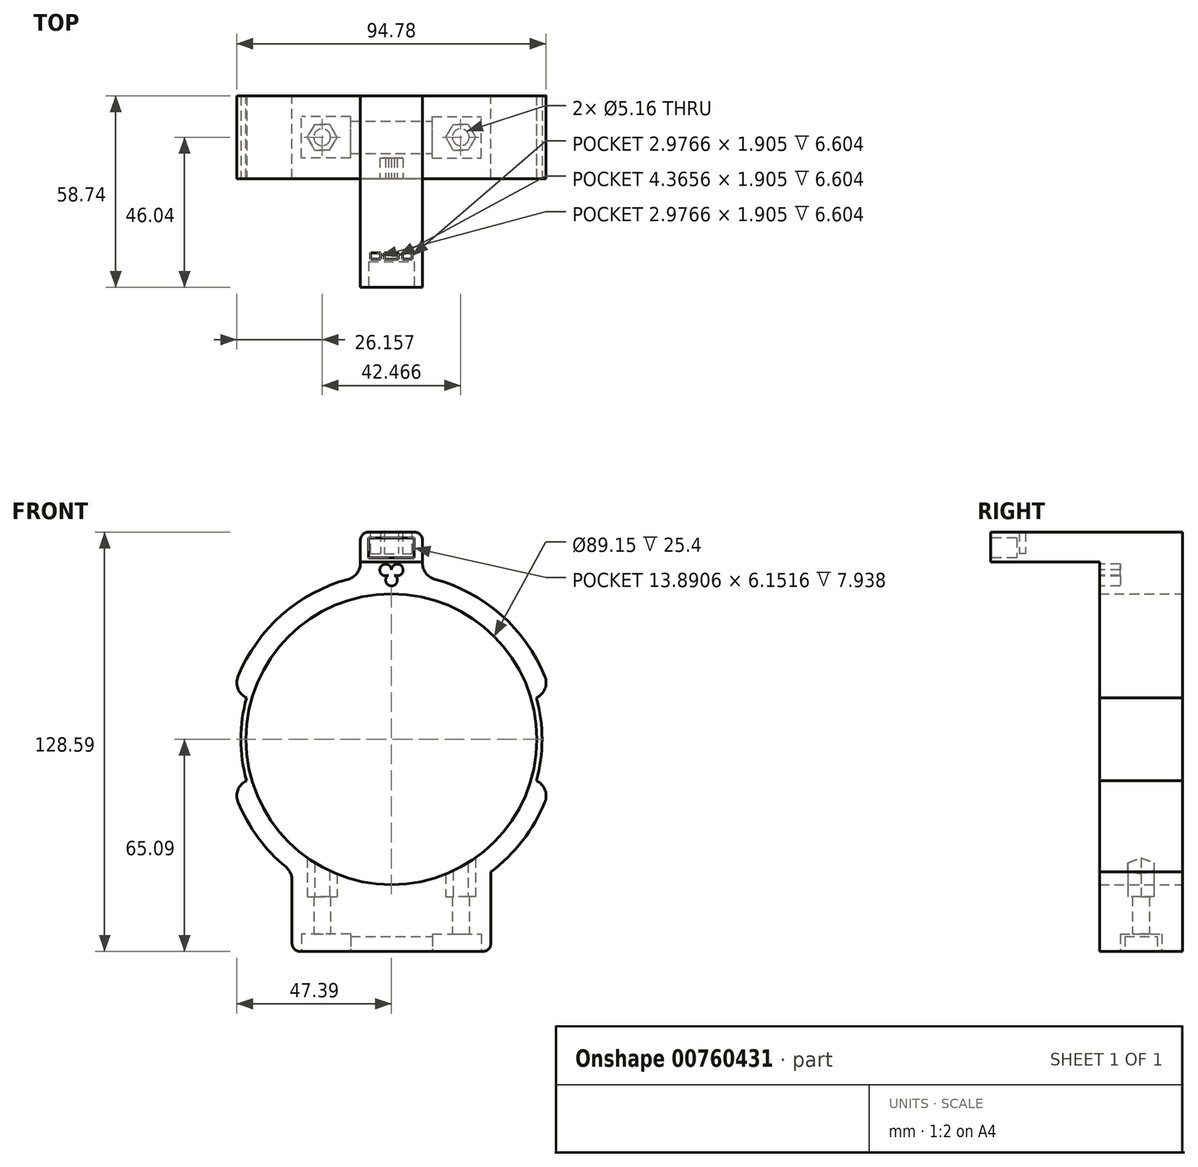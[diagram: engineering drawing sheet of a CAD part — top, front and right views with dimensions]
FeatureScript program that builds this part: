
annotation { "Feature Type Name" : "Feature", "Feature Type Description" : "" }
export const myFeature = defineFeature(function(context is Context, id is Id, definition is map)
    precondition{}
    {
        {
            var Q0;
            Q0=qCreatedBy(makeId("Front.planeOp"),FACE);
            var sketch = newSketch(context, id + "F0", { "sketchPlane" : qUnion([Q0])});
            skCircle(sketch, "E0", {"center": v(0, 0) * mm, "radius": 44.58 * mm});
            skCircle(sketch, "E1", {"center": v(0, 0) * mm, "radius": 50.8 * mm});
            skLineSegment(sketch, "E2.bottom", {"start": v(-9.52, 0) * mm, "end": v(9.53, 0) * mm});
            skLineSegment(sketch, "E2.top", {"start": v(-9.53, 63.5) * mm, "end": v(9.52, 63.5) * mm});
            skLineSegment(sketch, "E2.left", {"start": v(-9.52, 0) * mm, "end": v(-9.53, 63.5) * mm});
            skLineSegment(sketch, "E2.right", {"start": v(9.53, 0) * mm, "end": v(9.52, 63.5) * mm});
            skSolve(sketch);
        }
        {
            var Q0;
            {var subQ0=sQuery(id+"F0.wireOp",EDGE,"E2.left");var subQ1=sQuery(id+"F0.wireOp",EDGE,"E0");var subQ2=makeQuery(id+"F0.imprint","INTERSECT",VERTEX,{"derivedFrom":[subQ1,subQ0]});Q0=makeQuery(id+"F0.imprint","IMPRINT",FACE,{"disambiguationData":[TD([[makeQuery(id+"F0.imprint","IMPRINT",EDGE,{"disambiguationData":[TD([[subQ2,-1.0]])],"derivedFrom":subQ1}),-1.0]])]});}
            var Q1;
            {var subQ0=sQuery(id+"F0.wireOp",EDGE,"E2.left");var subQ1=sQuery(id+"F0.wireOp",EDGE,"E0");var subQ2=makeQuery(id+"F0.imprint","INTERSECT",VERTEX,{"derivedFrom":[subQ1,subQ0]});Q1=makeQuery(id+"F0.imprint","IMPRINT",FACE,{"disambiguationData":[TD([[makeQuery(id+"F0.imprint","IMPRINT",EDGE,{"disambiguationData":[TD([[subQ2,1.0]])],"derivedFrom":subQ1}),-1.0]])]});}
            var Q2;
            {var subQ5=sQuery(id+"F0.wireOp",EDGE,"E2.top");Q2=makeQuery(id+"F0.imprint","IMPRINT",FACE,{"disambiguationData":[TD([[makeQuery(id+"F0.imprint","IMPRINT",EDGE,{"derivedFrom":subQ5}),-1.0]])]});}
            extrude(context, id + "F1", {"entities" : qUnion([Q0, Q1, Q2]), "depth" : 25.4 * mm, "offsetDistance" : 25.4 * mm});
        }
        {
            var Q0;
            Q0=makeQuery(id+"F1.opExtrude","CAP_FACE",FACE,{"disambiguationData":[OSD([sQuery(id+"F0.wireOp",EDGE,"E0"),sQuery(id+"F0.wireOp",EDGE,"E1"),sQuery(id+"F0.wireOp",EDGE,"E2.top"),sQuery(id+"F0.wireOp",EDGE,"E2.left"),sQuery(id+"F0.wireOp",EDGE,"E2.right")])],"isStart":false});
            var sketch = newSketch(context, id + "F2", { "sketchPlane" : qUnion([Q0])});
            skCircle(sketch, "E3", {"center": v(1.79, 51.87) * mm, "radius": 1.79 * mm});
            skCircle(sketch, "E4.MirrorC", {"center": v(-1.79, 51.87) * mm, "radius": 1.79 * mm});
            skCircle(sketch, "E5", {"center": v(0, 48.78) * mm, "radius": 1.79 * mm});
            skSolve(sketch);
        }
        {
            var Q0;
            Q0=qSketchRegion(id+"F2",true);
            extrude(context, id + "F3", {"entities" : qUnion([Q0]), "operationType" : NewBodyOperationType.REMOVE, "oppositeDirection" : true, "depth" : 6.35 * mm, "offsetDistance" : 25.4 * mm});
        }
        {
            var Q0;
            Q0=qCreatedBy(makeId("Front.planeOp"),FACE);
            var sketch = newSketch(context, id + "F4", { "sketchPlane" : qUnion([Q0])});
            skLineSegment(sketch, "E6.bottom", {"start": v(30.48, -65.09) * mm, "end": v(-30.48, -65.09) * mm});
            skLineSegment(sketch, "E7", {"start": v(-30.48, -65.09) * mm, "end": v(-30.48, -40.64) * mm});
            skLineSegment(sketch, "E8", {"start": v(30.48, -65.09) * mm, "end": v(30.48, -40.64) * mm});
            skArc(sketch, "E9", {"start": v(-30.48, -40.64) * mm, "mid": v(0, -50.8) * mm, "end": v(30.48, -40.64) * mm});
            skLineSegment(sketch, "E10", {"start": v(0, -50.8) * mm, "end": v(0, -75.8) * mm, "construction": true});
            skLineSegment(sketch, "E11", {"start": v(10.8, -65.09) * mm, "end": v(10.8, -75.8) * mm, "construction": true});
            skLineSegment(sketch, "E12", {"start": v(-41.35, -44.45) * mm, "end": v(48.58, -44.45) * mm, "construction": true});
            skSolve(sketch);
        }
        {
            var Q0;
            Q0=qSketchRegion(id+"F4",true);
            extrude(context, id + "F5", {"entities" : qUnion([Q0]), "operationType" : NewBodyOperationType.ADD, "depth" : 25.4 * mm, "offsetDistance" : 25.4 * mm});
        }
        {
            var Q0;
            Q0=makeQuery(id+"F5.opExtrude","SWEPT_FACE",FACE,{"disambiguationData":[OSD([sQuery(id+"F4.wireOp",EDGE,"E6.bottom")])]});
            var sketch = newSketch(context, id + "F6", { "sketchPlane" : qUnion([Q0])});
            skLineSegment(sketch, "E13.bottom", {"start": v(12.5, 19.05) * mm, "end": v(27.58, 19.05) * mm});
            skLineSegment(sketch, "E13.top", {"start": v(12.5, 6.35) * mm, "end": v(27.58, 6.35) * mm});
            skLineSegment(sketch, "E13.left", {"start": v(12.5, 19.05) * mm, "end": v(12.5, 6.35) * mm});
            skLineSegment(sketch, "E13.right", {"start": v(27.58, 19.05) * mm, "end": v(27.58, 6.35) * mm});
            skLineSegment(sketch, "E14.MirrorCS", {"start": v(-12.5, 19.05) * mm, "end": v(-27.58, 19.05) * mm});
            skLineSegment(sketch, "E15.MirrorCS", {"start": v(-12.5, 19.05) * mm, "end": v(-12.5, 6.35) * mm});
            skLineSegment(sketch, "E16.MirrorCS", {"start": v(-12.5, 6.35) * mm, "end": v(-27.58, 6.35) * mm});
            skLineSegment(sketch, "E17.MirrorCS", {"start": v(-27.58, 19.05) * mm, "end": v(-27.58, 6.35) * mm});
            skPoint(sketch, "E18.centerSnap0", {"position": v(12.5, 12.7) * mm});
            skSolve(sketch);
        }
        {
            var Q0;
            Q0=qSketchRegion(id+"F6",true);
            extrude(context, id + "F7", {"entities" : qUnion([Q0]), "operationType" : NewBodyOperationType.REMOVE, "oppositeDirection" : true, "depth" : 5.36 * mm, "offsetDistance" : 25.4 * mm});
        }
        {
            var Q0;
            Q0=makeQuery(id+"F7.boolean.opBoolean","COPY",FACE,{"derivedFrom":makeQuery(id+"F7.opExtrude","CAP_FACE",FACE,{"disambiguationData":[OSD([sQuery(id+"F6.wireOp",EDGE,"E13.bottom"),sQuery(id+"F6.wireOp",EDGE,"E13.top"),sQuery(id+"F6.wireOp",EDGE,"E13.left"),sQuery(id+"F6.wireOp",EDGE,"E13.right")])],"isStart":false})});
            var sketch = newSketch(context, id + "F8", { "sketchPlane" : qUnion([Q0])});
            skCircle(sketch, "E19", {"center": v(21.23, 12.7) * mm, "radius": 2.58 * mm});
            skPoint(sketch, "E19.centerSnap0", {"position": v(12.5, 12.7) * mm});
            skCircle(sketch, "E20.MirrorC", {"center": v(-21.23, 12.7) * mm, "radius": 2.58 * mm});
            skSolve(sketch);
        }
        {
            var Q0;
            Q0=qSketchRegion(id+"F8",true);
            extrude(context, id + "F9", {"entities" : qUnion([Q0]), "operationType" : NewBodyOperationType.REMOVE, "oppositeDirection" : true, "depth" : 25.4 * mm, "offsetDistance" : 25.4 * mm});
        }
        {
            var Q0;
            Q0=qCreatedBy(makeId("Top.planeOp"),FACE);
            cPlane(context, id + "F10", {"entities" : qUnion([Q0]), "cplaneType" : CPlaneType.OFFSET, "offset" : 48.26 * mm, "oppositeDirection" : true, "width" : 152.4 * mm, "height" : 152.4 * mm});
        }
        {
            var Q0;
            Q0=qCreatedBy(id+"F10.planeOp",FACE);
            var sketch = newSketch(context, id + "F11", { "sketchPlane" : qUnion([Q0])});
            skCircle(sketch, "E21.cCircle", {"center": v(21.23, -12.7) * mm, "radius": 3.97 * mm, "construction": true});
            skLineSegment(sketch, "E21.0", {"start": v(23.52, -16.67) * mm, "end": v(18.94, -16.67) * mm});
            skLineSegment(sketch, "E21.1", {"start": v(18.94, -16.67) * mm, "end": v(16.65, -12.7) * mm});
            skLineSegment(sketch, "E21.2", {"start": v(16.65, -12.7) * mm, "end": v(18.94, -8.73) * mm});
            skLineSegment(sketch, "E21.3", {"start": v(18.94, -8.73) * mm, "end": v(23.52, -8.73) * mm});
            skLineSegment(sketch, "E21.4", {"start": v(23.52, -8.73) * mm, "end": v(25.82, -12.7) * mm});
            skLineSegment(sketch, "E21.5", {"start": v(25.82, -12.7) * mm, "end": v(23.52, -16.67) * mm});
            skPoint(sketch, "E21.0.midPoint", {"position": v(21.23, -16.67) * mm});
            skLineSegment(sketch, "E22.MirrorCS", {"start": v(-23.52, -16.67) * mm, "end": v(-18.94, -16.67) * mm});
            skLineSegment(sketch, "E23.MirrorCS", {"start": v(-18.94, -16.67) * mm, "end": v(-16.65, -12.7) * mm});
            skLineSegment(sketch, "E24.MirrorCS", {"start": v(-16.65, -12.7) * mm, "end": v(-18.94, -8.73) * mm});
            skLineSegment(sketch, "E25.MirrorCS", {"start": v(-18.94, -8.73) * mm, "end": v(-23.52, -8.73) * mm});
            skLineSegment(sketch, "E26.MirrorCS", {"start": v(-23.52, -8.73) * mm, "end": v(-25.82, -12.7) * mm});
            skLineSegment(sketch, "E27.MirrorCS", {"start": v(-25.82, -12.7) * mm, "end": v(-23.52, -16.67) * mm});
            skSolve(sketch);
        }
        {
            var Q0;
            Q0=qSketchRegion(id+"F11",true);
            extrude(context, id + "F12", {"entities" : qUnion([Q0]), "operationType" : NewBodyOperationType.REMOVE, "depth" : 25.4 * mm, "offsetDistance" : 25.4 * mm});
        }
        {
            var Q0;
            Q0=makeQuery(id+"F5.boolean.opBoolean","MERGE",FACE,{"derivedFrom":[makeQuery(id+"F1.opExtrude","CAP_FACE",FACE,{"disambiguationData":[OSD([sQuery(id+"F0.wireOp",EDGE,"E0"),sQuery(id+"F0.wireOp",EDGE,"E1"),sQuery(id+"F0.wireOp",EDGE,"E2.top"),sQuery(id+"F0.wireOp",EDGE,"E2.left"),sQuery(id+"F0.wireOp",EDGE,"E2.right")])],"isStart":false}),makeQuery(id+"F5.opExtrude","CAP_FACE",FACE,{"disambiguationData":[OSD([sQuery(id+"F4.wireOp",EDGE,"E6.bottom"),sQuery(id+"F4.wireOp",EDGE,"E7"),sQuery(id+"F4.wireOp",EDGE,"E8"),sQuery(id+"F4.wireOp",EDGE,"E9")])],"isStart":false})]});
            var sketch = newSketch(context, id + "F13", { "sketchPlane" : qUnion([Q0])});
            skLineSegment(sketch, "E28.bottom", {"start": v(-9.53, 63.5) * mm, "end": v(9.52, 63.5) * mm});
            skLineSegment(sketch, "E28.top", {"start": v(-9.53, 54.34) * mm, "end": v(9.52, 54.34) * mm});
            skLineSegment(sketch, "E28.left", {"start": v(-9.53, 63.5) * mm, "end": v(-9.53, 54.34) * mm});
            skLineSegment(sketch, "E28.right", {"start": v(9.52, 63.5) * mm, "end": v(9.52, 54.34) * mm});
            skSolve(sketch);
        }
        {
            var Q0;
            Q0 = qSketchRegion(id + "F13", true);
            extrude(context, id + "F14", {"entities" : qUnion([Q0]), "operationType" : NewBodyOperationType.ADD, "depth" : 33.34 * mm, "offsetDistance" : 25.4 * mm});
        }
        {
            var Q0;
            Q0=makeQuery(id+"F14.opExtrude","CAP_FACE",FACE,{"disambiguationData":[OSD([sQuery(id+"F13.wireOp",EDGE,"E28.bottom"),sQuery(id+"F13.wireOp",EDGE,"E28.top"),sQuery(id+"F13.wireOp",EDGE,"E28.left"),sQuery(id+"F13.wireOp",EDGE,"E28.right")])],"isStart":false});
            var sketch = newSketch(context, id + "F15", { "sketchPlane" : qUnion([Q0])});
            skLineSegment(sketch, "E29.bottom", {"start": v(-6.95, 61.77) * mm, "end": v(6.95, 61.77) * mm});
            skLineSegment(sketch, "E29.top", {"start": v(-6.95, 55.61) * mm, "end": v(6.95, 55.61) * mm});
            skLineSegment(sketch, "E29.left", {"start": v(-6.95, 61.77) * mm, "end": v(-6.95, 55.61) * mm});
            skLineSegment(sketch, "E29.right", {"start": v(6.95, 61.77) * mm, "end": v(6.95, 55.61) * mm});
            skSolve(sketch);
        }
        {
            var Q0;
            Q0 = qSketchRegion(id + "F15", true);
            extrude(context, id + "F16", {"entities" : qUnion([Q0]), "operationType" : NewBodyOperationType.REMOVE, "oppositeDirection" : true, "depth" : 7.94 * mm, "offsetDistance" : 25.4 * mm});
        }
        {
            var Q0;
            Q0=makeQuery(id+"F14.boolean.opBoolean","MERGE",FACE,{"derivedFrom":[makeQuery(id+"F1.opExtrude","SWEPT_FACE",FACE,{"disambiguationData":[OSD([sQuery(id+"F0.wireOp",EDGE,"E2.top")])]}),makeQuery(id+"F14.opExtrude","SWEPT_FACE",FACE,{"disambiguationData":[OSD([sQuery(id+"F13.wireOp",EDGE,"E28.bottom")])]})]});
            var sketch = newSketch(context, id + "F17", { "sketchPlane" : qUnion([Q0])});
            skLineSegment(sketch, "E30.bottom", {"start": v(-6.35, -48.1) * mm, "end": v(6.35, -48.1) * mm});
            skLineSegment(sketch, "E30.top", {"start": v(-6.35, -50) * mm, "end": v(6.35, -50) * mm});
            skLineSegment(sketch, "E30.left", {"start": v(-6.35, -48.1) * mm, "end": v(-6.35, -50) * mm});
            skLineSegment(sketch, "E30.right", {"start": v(6.35, -48.1) * mm, "end": v(6.35, -50) * mm});
            skSolve(sketch);
        }
        {
            var Q0;
            Q0 = qSketchRegion(id + "F17", true);
            extrude(context, id + "F18", {"entities" : qUnion([Q0]), "operationType" : NewBodyOperationType.REMOVE, "oppositeDirection" : true, "depth" : 6.6 * mm, "offsetDistance" : 25.4 * mm});
        }
        {
            var Q0;
            Q0=makeQuery(id+"F18.boolean.opBoolean","COPY",FACE,{"derivedFrom":makeQuery(id+"F18.opExtrude","CAP_FACE",FACE,{"disambiguationData":[OSD([sQuery(id+"F17.wireOp",EDGE,"E30.bottom"),sQuery(id+"F17.wireOp",EDGE,"E30.top"),sQuery(id+"F17.wireOp",EDGE,"E30.left"),sQuery(id+"F17.wireOp",EDGE,"E30.right")])],"isStart":false})});
            var sketch = newSketch(context, id + "F19", { "sketchPlane" : qUnion([Q0])});
            skLineSegment(sketch, "E31.bottom", {"start": v(-3.37, -48.1) * mm, "end": v(-2.18, -48.1) * mm});
            skLineSegment(sketch, "E31.top", {"start": v(-3.37, -50) * mm, "end": v(-2.18, -50) * mm});
            skLineSegment(sketch, "E31.left", {"start": v(-3.37, -48.1) * mm, "end": v(-3.37, -50) * mm});
            skLineSegment(sketch, "E31.right", {"start": v(-2.18, -48.1) * mm, "end": v(-2.18, -50) * mm});
            skLineSegment(sketch, "E32.MirrorCS", {"start": v(2.18, -48.1) * mm, "end": v(2.18, -50) * mm});
            skLineSegment(sketch, "E33.MirrorCS", {"start": v(3.37, -48.1) * mm, "end": v(3.37, -50) * mm});
            skLineSegment(sketch, "E34.MirrorCS", {"start": v(3.37, -48.1) * mm, "end": v(2.18, -48.1) * mm});
            skLineSegment(sketch, "E35.MirrorCS", {"start": v(3.37, -50) * mm, "end": v(2.18, -50) * mm});
            skSolve(sketch);
        }
        {
            var Q0;
            Q0 = qSketchRegion(id + "F19", true);
            extrude(context, id + "F20", {"entities" : qUnion([Q0]), "operationType" : NewBodyOperationType.ADD, "depth" : 6.6 * mm, "offsetDistance" : 25.4 * mm});
        }
        {
            var Q0;
            Q0=makeQuery(id+"F6.imprint","IMPRINT",FACE,{"disambiguationData":[TD([[makeQuery(id+"F6.imprint","IMPRINT",EDGE,{"derivedFrom":sQuery(id+"F6.wireOp",EDGE,"E13.bottom")}),1.0]])]});
            var sketch = newSketch(context, id + "F21", { "sketchPlane" : qUnion([Q0])});
            skLineSegment(sketch, "E36", {"start": v(-12.5, 12.7) * mm, "end": v(12.5, 12.7) * mm, "construction": true});
            skLineSegment(sketch, "E37.bottom", {"start": v(-12.5, 17.66) * mm, "end": v(12.5, 17.66) * mm});
            skLineSegment(sketch, "E37.top", {"start": v(-12.5, 7.74) * mm, "end": v(12.5, 7.74) * mm});
            skLineSegment(sketch, "E37.left", {"start": v(-12.5, 17.66) * mm, "end": v(-12.5, 7.74) * mm});
            skLineSegment(sketch, "E37.right", {"start": v(12.5, 17.66) * mm, "end": v(12.5, 7.74) * mm});
            skSolve(sketch);
        }
        {
            var Q0;
            Q0=makeQuery(id+"F21.imprint","IMPRINT",FACE,{"disambiguationData":[TD([[makeQuery(id+"F21.imprint","IMPRINT",EDGE,{"derivedFrom":sQuery(id+"F21.wireOp",EDGE,"E37.bottom")}),-1.0]])]});
            extrude(context, id + "F22", {"entities" : qUnion([Q0]), "operationType" : NewBodyOperationType.REMOVE, "oppositeDirection" : true, "depth" : 4.56 * mm, "offsetDistance" : 25.4 * mm});
        }
        {
            var Q0;
            Q0=makeQuery(id+"F2.imprint","IMPRINT",FACE,{"disambiguationData":[TD([[makeQuery(id+"F2.imprint","IMPRINT",EDGE,{"derivedFrom":makeQuery(id+"F1.opExtrude","CAP_EDGE",EDGE,{"disambiguationData":[OSD([sQuery(id+"F0.wireOp",EDGE,"E0")])],"isStart":false})}),-1.0]])]});
            var sketch = newSketch(context, id + "F23", { "sketchPlane" : qUnion([Q0])});
            skArc(sketch, "E38", {"start": v(44.38, -12.7) * mm, "mid": v(46.16, 0) * mm, "end": v(44.38, 12.7) * mm});
            skLineSegment(sketch, "E39.bottom", {"start": v(-55.64, 12.7) * mm, "end": v(-44.38, 12.7) * mm});
            skLineSegment(sketch, "E39.top", {"start": v(-55.64, -12.7) * mm, "end": v(-44.38, -12.7) * mm});
            skLineSegment(sketch, "E39.left", {"start": v(-55.64, 12.7) * mm, "end": v(-55.64, -12.7) * mm});
            skLineSegment(sketch, "E39.right", {"start": v(55.83, 12.7) * mm, "end": v(55.83, -12.7) * mm});
            skLineSegment(sketch, "E40.trimOffspring", {"start": v(44.38, 12.7) * mm, "end": v(55.83, 12.7) * mm});
            skLineSegment(sketch, "E41.trimOffspring", {"start": v(44.38, -12.7) * mm, "end": v(55.83, -12.7) * mm});
            skArc(sketch, "E42.trimOffspring", {"start": v(-44.38, 12.7) * mm, "mid": v(-46.16, 0) * mm, "end": v(-44.38, -12.7) * mm});
            skSolve(sketch);
        }
        {
            var Q0;
            Q0 = qSketchRegion(id + "F23", true);
            extrude(context, id + "F24", {"entities" : qUnion([Q0]), "operationType" : NewBodyOperationType.REMOVE, "oppositeDirection" : true, "depth" : 27.94 * mm, "offsetDistance" : 25.4 * mm});
        }
        {
            var Q0;
            {var subQ4=sQuery(id+"F0.wireOp",EDGE,"E2.left");var subQ7=sQuery(id+"F0.wireOp",EDGE,"E1");Q0=makeQuery(id+"F24.boolean.opBoolean","INTERSECT",EDGE,{"derivedFrom":[makeQuery(id+"F5.boolean.opBoolean","SPLIT",FACE,{"disambiguationData":[TD([makeQuery(id+"F1.opExtrude","SWEPT_FACE",FACE,{"disambiguationData":[OSD([subQ4])]})])],"derivedFrom":makeQuery(id+"F1.opExtrude","SWEPT_FACE",FACE,{"disambiguationData":[OSD([subQ7])]})}),makeQuery(id+"F24.opExtrude","SWEPT_FACE",FACE,{"disambiguationData":[OSD([sQuery(id+"F23.wireOp",EDGE,"E39.bottom")])]})]});}
            var Q1;
            {var subQ4=sQuery(id+"F0.wireOp",EDGE,"E2.left");var subQ7=sQuery(id+"F0.wireOp",EDGE,"E1");Q1=makeQuery(id+"F24.boolean.opBoolean","INTERSECT",EDGE,{"derivedFrom":[makeQuery(id+"F5.boolean.opBoolean","SPLIT",FACE,{"disambiguationData":[TD([makeQuery(id+"F1.opExtrude","SWEPT_FACE",FACE,{"disambiguationData":[OSD([subQ4])]})])],"derivedFrom":makeQuery(id+"F1.opExtrude","SWEPT_FACE",FACE,{"disambiguationData":[OSD([subQ7])]})}),makeQuery(id+"F24.opExtrude","SWEPT_FACE",FACE,{"disambiguationData":[OSD([sQuery(id+"F23.wireOp",EDGE,"E39.top")])]})]});}
            var Q2;
            {var subQ4=sQuery(id+"F0.wireOp",EDGE,"E2.right");var subQ7=sQuery(id+"F0.wireOp",EDGE,"E1");Q2=makeQuery(id+"F24.boolean.opBoolean","INTERSECT",EDGE,{"derivedFrom":[makeQuery(id+"F5.boolean.opBoolean","SPLIT",FACE,{"disambiguationData":[TD([makeQuery(id+"F1.opExtrude","SWEPT_FACE",FACE,{"disambiguationData":[OSD([subQ4])]})])],"derivedFrom":makeQuery(id+"F1.opExtrude","SWEPT_FACE",FACE,{"disambiguationData":[OSD([subQ7])]})}),makeQuery(id+"F24.opExtrude","SWEPT_FACE",FACE,{"disambiguationData":[OSD([sQuery(id+"F23.wireOp",EDGE,"E41.trimOffspring")])]})]});}
            var Q3;
            {var subQ4=sQuery(id+"F0.wireOp",EDGE,"E2.right");var subQ7=sQuery(id+"F0.wireOp",EDGE,"E1");Q3=makeQuery(id+"F24.boolean.opBoolean","INTERSECT",EDGE,{"derivedFrom":[makeQuery(id+"F5.boolean.opBoolean","SPLIT",FACE,{"disambiguationData":[TD([makeQuery(id+"F1.opExtrude","SWEPT_FACE",FACE,{"disambiguationData":[OSD([subQ4])]})])],"derivedFrom":makeQuery(id+"F1.opExtrude","SWEPT_FACE",FACE,{"disambiguationData":[OSD([subQ7])]})}),makeQuery(id+"F24.opExtrude","SWEPT_FACE",FACE,{"disambiguationData":[OSD([sQuery(id+"F23.wireOp",EDGE,"E40.trimOffspring")])]})]});}
            fillet(context, id + "F25", {"entities" : qUnion([Q0, Q1, Q2, Q3]), "radius" : 5.08 * mm, "tangentPropagation" : true, "allowEdgeOverflow" : false});
        }
        {
            var Q0;
            Q0=makeQuery(id+"F5.opExtrude","SWEPT_EDGE",EDGE,{"disambiguationData":[OSD([sQuery(id+"F4.wireOp",EDGE,"E6.bottom"),sQuery(id+"F4.wireOp",EDGE,"E8")])]});
            var Q1;
            Q1=makeQuery(id+"F5.opExtrude","SWEPT_EDGE",EDGE,{"disambiguationData":[OSD([sQuery(id+"F4.wireOp",EDGE,"E6.bottom"),sQuery(id+"F4.wireOp",EDGE,"E7")])]});
            fillet(context, id + "F26", {"entities" : qUnion([Q0, Q1]), "radius" : 2.54 * mm, "tangentPropagation" : true, "allowEdgeOverflow" : false});
        }
        {
            var Q0;
            Q0=makeQuery(id+"F14.boolean.opBoolean","MERGE",EDGE,{"derivedFrom":[makeQuery(id+"F1.opExtrude","SWEPT_EDGE",EDGE,{"disambiguationData":[OSD([sQuery(id+"F0.wireOp",EDGE,"E2.top"),sQuery(id+"F0.wireOp",EDGE,"E2.right")])]}),makeQuery(id+"F14.opExtrude","SWEPT_EDGE",EDGE,{"disambiguationData":[OSD([sQuery(id+"F13.wireOp",EDGE,"E28.bottom"),sQuery(id+"F13.wireOp",EDGE,"E28.right")])]})]});
            var Q1;
            Q1=makeQuery(id+"F14.boolean.opBoolean","MERGE",EDGE,{"derivedFrom":[makeQuery(id+"F1.opExtrude","SWEPT_EDGE",EDGE,{"disambiguationData":[OSD([sQuery(id+"F0.wireOp",EDGE,"E2.top"),sQuery(id+"F0.wireOp",EDGE,"E2.left")])]}),makeQuery(id+"F14.opExtrude","SWEPT_EDGE",EDGE,{"disambiguationData":[OSD([sQuery(id+"F13.wireOp",EDGE,"E28.bottom"),sQuery(id+"F13.wireOp",EDGE,"E28.left")])]})]});
            fillet(context, id + "F27", {"entities" : qUnion([Q0, Q1]), "radius" : 2.54 * mm, "tangentPropagation" : true, "allowEdgeOverflow" : false});
        }
        {
            var Q0;
            Q0=makeQuery(id+"F5.opExtrude","SWEPT_EDGE",EDGE,{"disambiguationData":[OSD([sQuery(id+"F4.wireOp",EDGE,"E8"),sQuery(id+"F4.wireOp",EDGE,"E9")])]});
            var Q1;
            Q1=makeQuery(id+"F5.opExtrude","SWEPT_EDGE",EDGE,{"disambiguationData":[OSD([sQuery(id+"F4.wireOp",EDGE,"E7"),sQuery(id+"F4.wireOp",EDGE,"E9")])]});
            var Q2;
            Q2=makeQuery(id+"F1.opExtrude","SWEPT_EDGE",EDGE,{"disambiguationData":[OSD([sQuery(id+"F0.wireOp",EDGE,"E1"),sQuery(id+"F0.wireOp",EDGE,"E2.left")])]});
            var Q3;
            Q3=makeQuery(id+"F1.opExtrude","SWEPT_EDGE",EDGE,{"disambiguationData":[OSD([sQuery(id+"F0.wireOp",EDGE,"E1"),sQuery(id+"F0.wireOp",EDGE,"E2.right")])]});
            fillet(context, id + "F28", {"entities" : qUnion([Q0, Q1, Q2, Q3]), "radius" : 5.08 * mm, "tangentPropagation" : true, "allowEdgeOverflow" : false});
        }
    });
